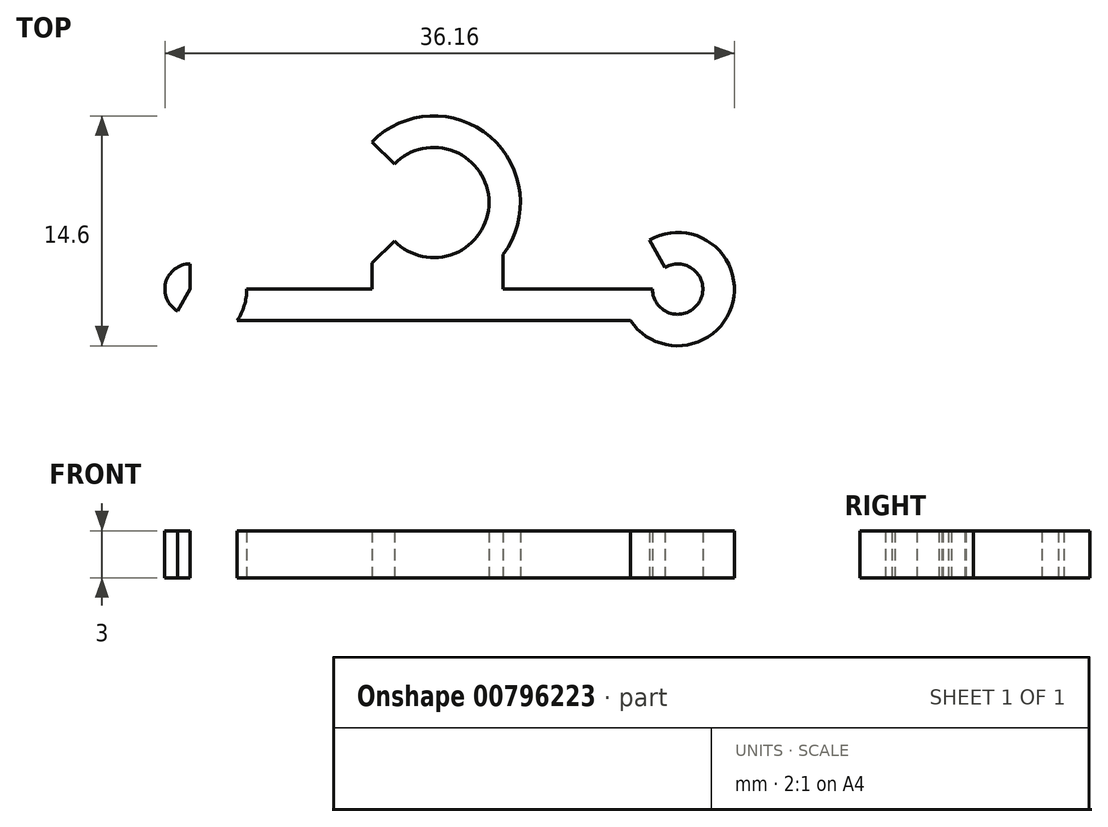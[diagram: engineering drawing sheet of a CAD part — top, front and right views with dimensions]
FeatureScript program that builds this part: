
annotation { "Feature Type Name" : "Feature", "Feature Type Description" : "" }
export const myFeature = defineFeature(function(context is Context, id is Id, definition is map)
    precondition{}
    {
        {
            var Q0;
            Q0=qCreatedBy(makeId("Top.planeOp"),FACE);
            var sketch = newSketch(context, id + "F0", { "sketchPlane" : qUnion([Q0])});
            skCircle(sketch, "E0", {"center": v(0, 0) * mm, "radius": 3.5 * mm});
            skCircle(sketch, "E1.0", {"center": v(0, 0) * mm, "radius": 5.5 * mm});
            skLineSegment(sketch, "E2", {"start": v(0, 0) * mm, "end": v(0, -23.5) * mm, "construction": true});
            skCircle(sketch, "E3.cCircle", {"center": v(0, 2.1) * mm, "radius": 9.6 * mm, "construction": true});
            skLineSegment(sketch, "E3.0", {"start": v(-16.64, -7.5) * mm, "end": v(0, 21.32) * mm});
            skLineSegment(sketch, "E3.1", {"start": v(0, 21.32) * mm, "end": v(16.64, -7.5) * mm});
            skLineSegment(sketch, "E3.2", {"start": v(16.64, -7.5) * mm, "end": v(-16.64, -7.5) * mm});
            skPoint(sketch, "E3.0.midPoint", {"position": v(-8.32, 6.9) * mm});
            skLineSegment(sketch, "E4", {"start": v(-15.48, -5.5) * mm, "end": v(15.48, -5.5) * mm});
            skCircle(sketch, "E5", {"center": v(-15.48, -5.5) * mm, "radius": 3.6 * mm});
            skCircle(sketch, "E6", {"center": v(-15.48, -5.5) * mm, "radius": 1.6 * mm});
            skLineSegment(sketch, "E7", {"start": v(-16.64, -7.5) * mm, "end": v(-19.39, -7.5) * mm});
            skLineSegment(sketch, "E8", {"start": v(-15.48, -5.5) * mm, "end": v(-15.48, 0) * mm});
            skCircle(sketch, "E9", {"center": v(15.48, -5.5) * mm, "radius": 1.6 * mm});
            skCircle(sketch, "E10", {"center": v(15.48, -5.5) * mm, "radius": 3.6 * mm});
            skPoint(sketch, "E11", {"position": v(13.88, -5.5) * mm});
            skLineSegment(sketch, "E12", {"start": v(16.64, -7.5) * mm, "end": v(24.75, -7.5) * mm});
            skLineSegment(sketch, "E13", {"start": v(-3.94, -3.84) * mm, "end": v(-3.94, -5.5) * mm});
            skLineSegment(sketch, "E14", {"start": v(4.4, -3.3) * mm, "end": v(4.4, -5.5) * mm});
            skLineSegment(sketch, "E15", {"start": v(0, 0) * mm, "end": v(-3.94, -3.84) * mm});
            skLineSegment(sketch, "E16", {"start": v(0, 0) * mm, "end": v(-3.94, 3.84) * mm});
            skSolve(sketch);
        }
        {
            var Q0;
            {var subQ6=sQuery(id+"F0.wireOp",EDGE,"E10");var subQ7=sQuery(id+"F0.wireOp",EDGE,"E3.2");var subQ8=makeQuery(id+"F0.imprint","INTERSECT",VERTEX,{"derivedFrom":[subQ7,subQ6]});Q0=makeQuery(id+"F0.imprint","IMPRINT",FACE,{"disambiguationData":[TD([[makeQuery(id+"F0.imprint","IMPRINT",EDGE,{"disambiguationData":[TD([[subQ8,-1.0]])],"derivedFrom":subQ7}),-1.0]])]});}
            var Q1;
            {var subQ3=sQuery(id+"F0.wireOp",EDGE,"E4");var subQ5=sQuery(id+"F0.wireOp",EDGE,"E6");var subQ6=makeQuery(id+"F0.imprint","INTERSECT",VERTEX,{"derivedFrom":[subQ3,subQ5]});Q1=makeQuery(id+"F0.imprint","IMPRINT",FACE,{"disambiguationData":[TD([[makeQuery(id+"F0.imprint","IMPRINT",EDGE,{"disambiguationData":[TD([[subQ6,-1.0]])],"derivedFrom":subQ3}),-1.0]])]});}
            var Q2;
            {var subQ0=sQuery(id+"F0.wireOp",EDGE,"E5");var subQ1=sQuery(id+"F0.wireOp",EDGE,"E8");var subQ2=makeQuery(id+"F0.imprint","INTERSECT",VERTEX,{"derivedFrom":[subQ1,subQ0]});Q2=makeQuery(id+"F0.imprint","IMPRINT",FACE,{"disambiguationData":[TD([[makeQuery(id+"F0.imprint","IMPRINT",EDGE,{"disambiguationData":[TD([[subQ2,1.0]])],"derivedFrom":subQ1}),1.0]])]});}
            var Q3;
            {var subQ3=sQuery(id+"F0.wireOp",EDGE,"E10");var subQ7=sQuery(id+"F0.wireOp",EDGE,"E4");var subQ9=makeQuery(id+"F0.imprint","INTERSECT",VERTEX,{"derivedFrom":[subQ7,subQ3]});Q3=makeQuery(id+"F0.imprint","IMPRINT",FACE,{"disambiguationData":[TD([[makeQuery(id+"F0.imprint","IMPRINT",EDGE,{"disambiguationData":[TD([[subQ9,-1.0]])],"derivedFrom":subQ7}),-1.0]])]});}
            var Q4;
            {var subQ1=sQuery(id+"F0.wireOp",EDGE,"E3.1");var subQ5=sQuery(id+"F0.wireOp",EDGE,"E10");var subQ7=makeQuery(id+"F0.imprint","INTERSECT",VERTEX,{"derivedFrom":[subQ1,subQ5]});Q4=makeQuery(id+"F0.imprint","IMPRINT",FACE,{"disambiguationData":[TD([[makeQuery(id+"F0.imprint","IMPRINT",EDGE,{"disambiguationData":[TD([[subQ7,-1.0]])],"derivedFrom":subQ1}),1.0]])]});}
            var Q5;
            {var subQ5=sQuery(id+"F0.wireOp",EDGE,"E15");var subQ7=sQuery(id+"F0.wireOp",EDGE,"E0");var subQ8=makeQuery(id+"F0.imprint","INTERSECT",VERTEX,{"derivedFrom":[subQ7,subQ5]});Q5=makeQuery(id+"F0.imprint","IMPRINT",FACE,{"disambiguationData":[TD([[makeQuery(id+"F0.imprint","IMPRINT",EDGE,{"disambiguationData":[TD([[subQ8,-1.0]])],"derivedFrom":subQ7}),-1.0]])]});}
            var Q6;
            {var subQ0=sQuery(id+"F0.wireOp",EDGE,"E13");Q6=makeQuery(id+"F0.imprint","IMPRINT",FACE,{"disambiguationData":[TD([[makeQuery(id+"F0.imprint","IMPRINT",EDGE,{"derivedFrom":subQ0}),1.0]])]});}
            var Q7;
            {var subQ0=sQuery(id+"F0.wireOp",EDGE,"E14");Q7=makeQuery(id+"F0.imprint","IMPRINT",FACE,{"disambiguationData":[TD([[makeQuery(id+"F0.imprint","IMPRINT",EDGE,{"derivedFrom":subQ0}),-1.0]])]});}
            var Q8;
            {var subQ0=sQuery(id+"F0.wireOp",EDGE,"E12");var subQ3=sQuery(id+"F0.wireOp",EDGE,"E10");var subQ5=makeQuery(id+"F0.imprint","INTERSECT",VERTEX,{"derivedFrom":[subQ3,subQ0]});Q8=makeQuery(id+"F0.imprint","IMPRINT",FACE,{"disambiguationData":[TD([[makeQuery(id+"F0.imprint","IMPRINT",EDGE,{"disambiguationData":[TD([[subQ5,1.0]])],"derivedFrom":subQ3}),1.0]])]});}
            var Q9;
            {var subQ0=sQuery(id+"F0.wireOp",EDGE,"E7");var subQ3=sQuery(id+"F0.wireOp",EDGE,"E5");var subQ5=makeQuery(id+"F0.imprint","INTERSECT",VERTEX,{"derivedFrom":[subQ0,subQ3]});Q9=makeQuery(id+"F0.imprint","IMPRINT",FACE,{"disambiguationData":[TD([[makeQuery(id+"F0.imprint","IMPRINT",EDGE,{"disambiguationData":[TD([[subQ5,1.0]])],"derivedFrom":subQ3}),-1.0]])]});}
            extrude(context, id + "F1", {"entities" : qUnion([Q0, Q1, Q2, Q3, Q4, Q5, Q6, Q7, Q8, Q9]), "depth" : 3 * mm, "offsetDistance" : 25 * mm});
        }
    });
